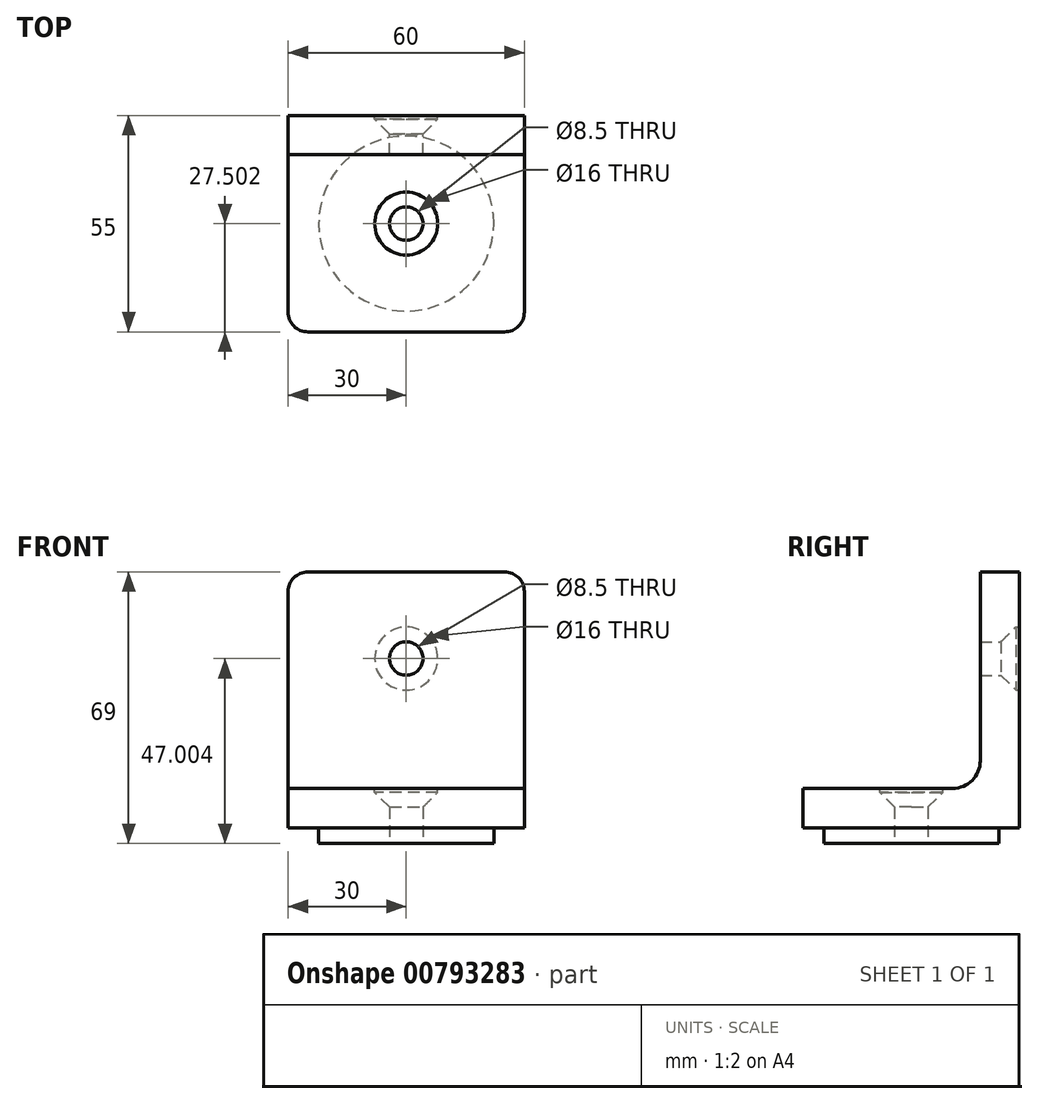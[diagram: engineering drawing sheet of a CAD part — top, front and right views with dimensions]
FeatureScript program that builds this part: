
annotation { "Feature Type Name" : "Feature", "Feature Type Description" : "" }
export const myFeature = defineFeature(function(context is Context, id is Id, definition is map)
    precondition{}
    {
        {
            var Q0;
            Q0=qCreatedBy(makeId("Right.planeOp"),FACE);
            var sketch = newSketch(context, id + "F0", { "sketchPlane" : qUnion([Q0])});
            skLineSegment(sketch, "E0", {"start": v(32.36, 47.91) * mm, "end": v(32.36, -17.09) * mm});
            skLineSegment(sketch, "E1", {"start": v(32.36, -17.09) * mm, "end": v(-22.64, -17.09) * mm});
            skLineSegment(sketch, "E2", {"start": v(-22.64, -17.09) * mm, "end": v(-22.64, -7.09) * mm});
            skLineSegment(sketch, "E3", {"start": v(-22.64, -7.09) * mm, "end": v(22.36, -7.09) * mm});
            skLineSegment(sketch, "E4", {"start": v(32.36, 47.91) * mm, "end": v(22.36, 47.91) * mm});
            skLineSegment(sketch, "E5", {"start": v(22.36, 47.91) * mm, "end": v(22.36, -7.09) * mm});
            skSolve(sketch);
        }
        {
            var Q0;
            Q0 = qSketchRegion(id + "F0", true);
            extrude(context, id + "F1", {"entities" : qUnion([Q0]), "depth" : 60 * mm, "offsetDistance" : 25 * mm});
        }
        {
            var Q0;
            Q0=makeQuery(id+"F1.opExtrude","SWEPT_FACE",FACE,{"disambiguationData":[OSD([sQuery(id+"F0.wireOp",EDGE,"E1")])]});
            var sketch = newSketch(context, id + "F2", { "sketchPlane" : qUnion([Q0])});
            skCircle(sketch, "E6", {"center": v(30, -4.86) * mm, "radius": 22.25 * mm});
            skPoint(sketch, "E6.centerSnap0", {"position": v(0, -4.86) * mm});
            skPoint(sketch, "E6.centerSnap1", {"position": v(30, -32.36) * mm});
            skSolve(sketch);
        }
        {
            var Q0;
            Q0 = qSketchRegion(id + "F2", true);
            extrude(context, id + "F3", {"entities" : qUnion([Q0]), "operationType" : NewBodyOperationType.ADD, "depth" : 4 * mm, "offsetDistance" : 25 * mm});
        }
        {
            var Q0;
            Q0=makeQuery(id+"F3.opExtrude","CAP_FACE",FACE,{"disambiguationData":[OSD([sQuery(id+"F2.wireOp",EDGE,"E6")])],"isStart":false});
            var sketch = newSketch(context, id + "F4", { "sketchPlane" : qUnion([Q0])});
            skCircle(sketch, "E7", {"center": v(30, -4.86) * mm, "radius": 4.25 * mm});
            skSolve(sketch);
        }
        {
            var Q0;
            Q0 = qSketchRegion(id + "F4", true);
            extrude(context, id + "F5", {"entities" : qUnion([Q0]), "operationType" : NewBodyOperationType.REMOVE, "oppositeDirection" : true, "depth" : 25 * mm, "offsetDistance" : 25 * mm});
        }
        {
            var Q0;
            Q0=makeQuery(id+"F1.opExtrude","SWEPT_FACE",FACE,{"disambiguationData":[OSD([sQuery(id+"F0.wireOp",EDGE,"E3")])]});
            var sketch = newSketch(context, id + "F6", { "sketchPlane" : qUnion([Q0])});
            skCircle(sketch, "E8", {"center": v(30, 4.86) * mm, "radius": 8 * mm});
            skSolve(sketch);
        }
        {
            var Q0;
            Q0 = qSketchRegion(id + "F6", true);
            extrude(context, id + "F7", {"entities" : qUnion([Q0]), "operationType" : NewBodyOperationType.REMOVE, "oppositeDirection" : true, "depth" : 1 * mm, "offsetDistance" : 25 * mm});
        }
        {
            var Q0;
            Q0=makeQuery(id+"F7.boolean.opBoolean","INTERSECT",EDGE,{"derivedFrom":[makeQuery(id+"F5.boolean.opBoolean","COPY",FACE,{"derivedFrom":makeQuery(id+"F5.opExtrude","SWEPT_FACE",FACE,{"disambiguationData":[OSD([sQuery(id+"F4.wireOp",EDGE,"E7")])]})}),makeQuery(id+"F7.opExtrude","CAP_FACE",FACE,{"disambiguationData":[OSD([sQuery(id+"F6.wireOp",EDGE,"E8")])],"isStart":false})]});
            chamfer(context, id + "F8", {"entities" : qUnion([Q0]), "width" : 3.75 * mm, "tangentPropagation" : true});
        }
        {
            var Q0;
            Q0=makeQuery(id+"F1.opExtrude","SWEPT_FACE",FACE,{"disambiguationData":[OSD([sQuery(id+"F0.wireOp",EDGE,"E0")])]});
            var sketch = newSketch(context, id + "F9", { "sketchPlane" : qUnion([Q0])});
            skCircle(sketch, "E9", {"center": v(-30, 25.91) * mm, "radius": 4.25 * mm});
            skPoint(sketch, "E9.centerSnap0", {"position": v(-30, 47.91) * mm});
            skSolve(sketch);
        }
        {
            var Q0;
            Q0 = qSketchRegion(id + "F9", true);
            extrude(context, id + "F10", {"entities" : qUnion([Q0]), "operationType" : NewBodyOperationType.REMOVE, "oppositeDirection" : true, "depth" : 25 * mm, "offsetDistance" : 25 * mm});
        }
        {
            var Q0;
            Q0=makeQuery(id+"F1.opExtrude","SWEPT_FACE",FACE,{"disambiguationData":[OSD([sQuery(id+"F0.wireOp",EDGE,"E0")])]});
            var sketch = newSketch(context, id + "F11", { "sketchPlane" : qUnion([Q0])});
            skCircle(sketch, "E10", {"center": v(-30, 25.91) * mm, "radius": 8 * mm});
            skSolve(sketch);
        }
        {
            var Q0;
            Q0 = qSketchRegion(id + "F11", true);
            extrude(context, id + "F12", {"entities" : qUnion([Q0]), "operationType" : NewBodyOperationType.REMOVE, "oppositeDirection" : true, "depth" : 1 * mm, "offsetDistance" : 25 * mm});
        }
        {
            var Q0;
            Q0=makeQuery(id+"F12.boolean.opBoolean","INTERSECT",EDGE,{"derivedFrom":[makeQuery(id+"F10.boolean.opBoolean","COPY",FACE,{"derivedFrom":makeQuery(id+"F10.opExtrude","SWEPT_FACE",FACE,{"disambiguationData":[OSD([sQuery(id+"F9.wireOp",EDGE,"E9")])]})}),makeQuery(id+"F12.opExtrude","CAP_FACE",FACE,{"disambiguationData":[OSD([sQuery(id+"F11.wireOp",EDGE,"E10")])],"isStart":false})]});
            chamfer(context, id + "F13", {"entities" : qUnion([Q0]), "width" : 3.75 * mm, "tangentPropagation" : true});
        }
        {
            var Q0;
            Q0=makeQuery(id+"F1.opExtrude","CAP_EDGE",EDGE,{"disambiguationData":[OSD([sQuery(id+"F0.wireOp",EDGE,"E2")])],"isStart":true});
            var Q1;
            Q1=makeQuery(id+"F1.opExtrude","CAP_EDGE",EDGE,{"disambiguationData":[OSD([sQuery(id+"F0.wireOp",EDGE,"E2")])],"isStart":false});
            var Q2;
            Q2=makeQuery(id+"F1.opExtrude","CAP_EDGE",EDGE,{"disambiguationData":[OSD([sQuery(id+"F0.wireOp",EDGE,"E4")])],"isStart":false});
            var Q3;
            Q3=makeQuery(id+"F1.opExtrude","CAP_EDGE",EDGE,{"disambiguationData":[OSD([sQuery(id+"F0.wireOp",EDGE,"E4")])],"isStart":true});
            fillet(context, id + "F14", {"entities" : qUnion([Q0, Q1, Q2, Q3]), "radius" : 5 * mm, "tangentPropagation" : true, "allowEdgeOverflow" : false});
        }
        {
            var Q0;
            Q0=makeQuery(id+"F1.opExtrude","SWEPT_EDGE",EDGE,{"disambiguationData":[OSD([sQuery(id+"F0.wireOp",EDGE,"E3"),sQuery(id+"F0.wireOp",EDGE,"E5")])]});
            fillet(context, id + "F15", {"entities" : qUnion([Q0]), "radius" : 7 * mm, "tangentPropagation" : true, "allowEdgeOverflow" : false});
        }
    });
